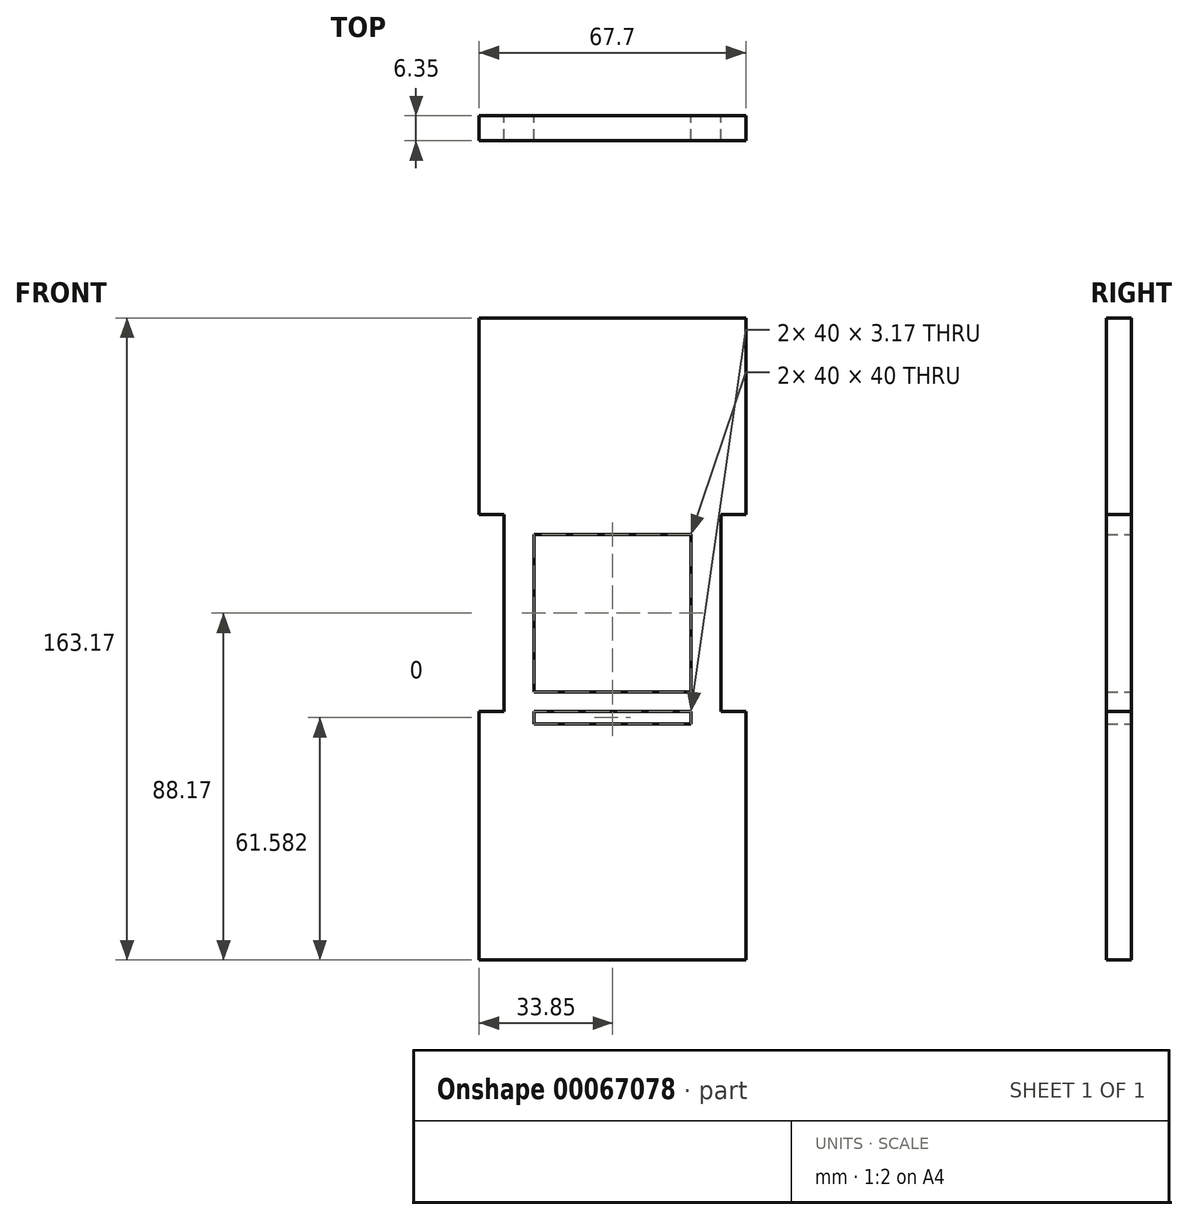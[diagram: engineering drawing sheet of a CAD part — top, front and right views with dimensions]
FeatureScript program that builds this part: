
annotation { "Feature Type Name" : "Feature", "Feature Type Description" : "" }
export const myFeature = defineFeature(function(context is Context, id is Id, definition is map)
    precondition{}
    {
        {
            var Q0;
            Q0=qCreatedBy(makeId("Front.planeOp"),FACE);
            var sketch = newSketch(context, id + "F0", { "sketchPlane" : qUnion([Q0])});
            skLineSegment(sketch, "E0.bottom", {"start": v(-33.85, 0) * mm, "end": v(33.85, 0) * mm});
            skLineSegment(sketch, "E0.top", {"start": v(-33.85, -163.18) * mm, "end": v(33.85, -163.18) * mm});
            skLineSegment(sketch, "E0.left", {"start": v(-33.85, 0) * mm, "end": v(-33.85, -163.18) * mm});
            skLineSegment(sketch, "E0.right", {"start": v(33.85, 0) * mm, "end": v(33.85, -163.18) * mm});
            skLineSegment(sketch, "E1.bottom", {"start": v(-20, -100) * mm, "end": v(20, -100) * mm});
            skLineSegment(sketch, "E1.top", {"start": v(-20, -103.18) * mm, "end": v(20, -103.18) * mm});
            skLineSegment(sketch, "E1.left", {"start": v(-20, -100) * mm, "end": v(-20, -103.17) * mm});
            skLineSegment(sketch, "E1.right", {"start": v(20, -100) * mm, "end": v(20, -103.17) * mm});
            skLineSegment(sketch, "E2.bottom", {"start": v(-20, -55) * mm, "end": v(20, -55) * mm});
            skLineSegment(sketch, "E2.top", {"start": v(-20, -95) * mm, "end": v(20, -95) * mm});
            skLineSegment(sketch, "E2.left", {"start": v(-20, -55) * mm, "end": v(-20, -95) * mm});
            skLineSegment(sketch, "E2.right", {"start": v(20, -55) * mm, "end": v(20, -95) * mm});
            skLineSegment(sketch, "E3.bottom", {"start": v(-33.85, -50) * mm, "end": v(-27.5, -50) * mm});
            skLineSegment(sketch, "E3.top", {"start": v(-33.85, -100) * mm, "end": v(-27.5, -100) * mm});
            skLineSegment(sketch, "E3.left", {"start": v(-33.85, -50) * mm, "end": v(-33.85, -100) * mm});
            skLineSegment(sketch, "E3.right", {"start": v(-27.5, -50) * mm, "end": v(-27.5, -100) * mm});
            skLineSegment(sketch, "E4.bottom", {"start": v(33.85, -50) * mm, "end": v(27.5, -50) * mm});
            skLineSegment(sketch, "E4.top", {"start": v(33.85, -100) * mm, "end": v(27.5, -100) * mm});
            skLineSegment(sketch, "E4.left", {"start": v(33.85, -50) * mm, "end": v(33.85, -100) * mm});
            skLineSegment(sketch, "E4.right", {"start": v(27.5, -50) * mm, "end": v(27.5, -100) * mm});
            skLineSegment(sketch, "E5", {"start": v(20, -103.18) * mm, "end": v(33.85, -103.18) * mm, "construction": true});
            skLineSegment(sketch, "E6", {"start": v(-20, -103.18) * mm, "end": v(-33.85, -103.18) * mm, "construction": true});
            skSolve(sketch);
        }
        {
            var Q0;
            {var subQ0=sQuery(id+"F0.wireOp",EDGE,"E0.bottom");Q0=makeQuery(id+"F0.imprint","IMPRINT",FACE,{"disambiguationData":[TD([[makeQuery(id+"F0.imprint","IMPRINT",EDGE,{"derivedFrom":subQ0}),-1.0]])]});}
            extrude(context, id + "F1", {"entities" : qUnion([Q0]), "depth" : 6.35 * mm});
        }
        {
            var Q0;
            Q0=makeQuery(id+"F1.opExtrude","SWEPT_BODY",BODY,{"disambiguationData":[OSD([sQuery(id+"F0.wireOp",EDGE,"E0.bottom"),sQuery(id+"F0.wireOp",EDGE,"E0.top"),sQuery(id+"F0.wireOp",EDGE,"E0.left"),sQuery(id+"F0.wireOp",EDGE,"E0.right"),sQuery(id+"F0.wireOp",EDGE,"E1.bottom"),sQuery(id+"F0.wireOp",EDGE,"E1.top"),sQuery(id+"F0.wireOp",EDGE,"E1.left"),sQuery(id+"F0.wireOp",EDGE,"E1.right"),sQuery(id+"F0.wireOp",EDGE,"E2.bottom"),sQuery(id+"F0.wireOp",EDGE,"E2.top"),sQuery(id+"F0.wireOp",EDGE,"E2.left"),sQuery(id+"F0.wireOp",EDGE,"E2.right"),sQuery(id+"F0.wireOp",EDGE,"E3.bottom"),sQuery(id+"F0.wireOp",EDGE,"E3.top"),sQuery(id+"F0.wireOp",EDGE,"E3.right"),sQuery(id+"F0.wireOp",EDGE,"E4.bottom"),sQuery(id+"F0.wireOp",EDGE,"E4.top"),sQuery(id+"F0.wireOp",EDGE,"E4.right")])]});
            transform(context, id + "F2", {"entities" : qUnion([Q0]), "transformType" : TransformType.TRANSLATION_3D, "dx" : 0 * mm, "dy" : 0 * mm, "dz" : 0 * mm, "makeCopy" : true});
        }
    });
